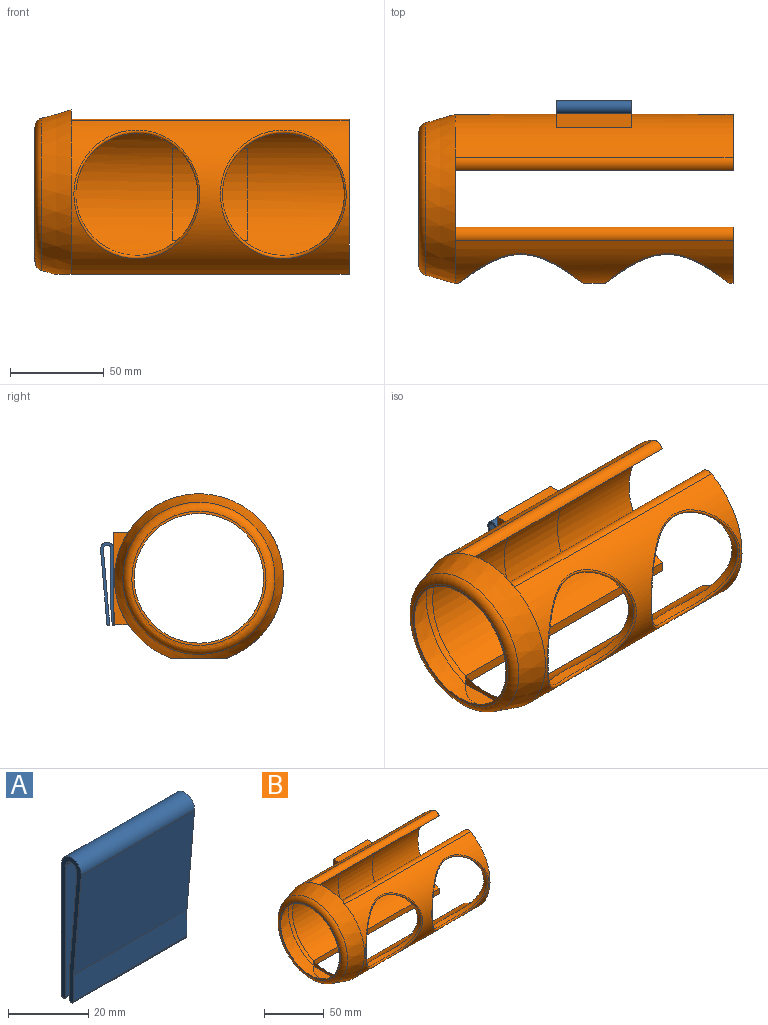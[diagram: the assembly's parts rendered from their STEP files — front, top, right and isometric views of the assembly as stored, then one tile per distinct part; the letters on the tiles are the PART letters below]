
ASSEMBLY  parts=2 mates=1
PART A: 18 faces, bbox 40x7x44.3 mm
  f0: plane 40x15.94mm, normal (0,-1,0), area 637.5mm2, adj f1,f8,f13,f17
  f1: cylinder r=0.75mm len=15.94mm, axis (-1,0,0), area 37.5mm2, adj f0,f2,f13,f17
  f2: plane 40x15.94mm, normal (0,1,0), area 637.5mm2, adj f1,f12,f13,f17
  f3: plane 40x31.9mm, normal (0,-1,-0.08), area 1280.5mm2, adj f4,f12,f13,f14
  f4: plane 40x8.03mm, normal (0,-1,0), area 321.1mm2, adj f3,f5,f13,f14
  f5: cylinder r=0.75mm len=40mm, axis (-1,0,0), area 94.6mm2, adj f4,f6,f13,f14
  f6: plane 40x8.03mm, normal (0,1,0), area 321.1mm2, adj f5,f7,f13,f14
  f7: plane 40x31.97mm, normal (0,1,0.08), area 1283.4mm2, adj f6,f8,f13,f14
  f8: cylinder r=2mm len=40mm, axis (-1,0,0), area 251.3mm2, adj f0,f7,f9,f13,f14,f15
  f9: plane 40x17.26mm, normal (0,-1,0), area 690.4mm2, adj f8,f10,f14,f16
  f10: cylinder r=0.75mm len=17.26mm, axis (-1,0,0), area 40.7mm2, adj f9,f11,f14,f16
  f11: plane 40x17.26mm, normal (0,1,0), area 690.4mm2, adj f10,f12,f14,f16
  f12: cylinder r=3.5mm len=40mm, axis (-1,0,0), area 442.7mm2, adj f2,f3,f11,f13,f14,f15
  f13: plane 44.25x7mm, normal (1,0,0), area 134.9mm2, adj f0,f1,f2,f3,f4,f5,f6,f7
  f14: plane 44.25x7mm, normal (-1,0,0), area 134.9mm2, adj f3,f4,f5,f6,f7,f8,f9,f10
  f15: plane 6.8x1.5mm, normal (0,0,-1), area 10.2mm2, adj f8,f12,f16,f17
  f16: plane 40.75x1.5mm, normal (1,0,0), area 60.9mm2, adj f9,f10,f11,f15
  f17: plane 40.75x1.5mm, normal (-1,0,0), area 60.9mm2, adj f0,f1,f2,f15
PART B: 27 faces, bbox 167.2x90.4x90 mm
  f0: cylinder r=40mm len=148mm, axis (-1,0,0), area 11937.5mm2, adj f8,f9,f12,f15,f26
  f1: cylinder r=45mm len=148mm, axis (-1,0,0), area 13193.9mm2, adj f4,f9,f12,f15,f22,f23,f24,f25
  f2: cylinder r=40mm len=148mm, axis (-1,0,0), area 6613.2mm2, adj f6,f8,f11,f14,f17,f18
  f3: cylinder r=45mm len=148mm, axis (-1,0,0), area 7367.5mm2, adj f4,f6,f11,f14,f19,f20
  f4: cone r=39.5mm half-angle=16deg, axis (1,0,0), area 4173.1mm2, adj f1,f3,f10,f13,f16
  f5: plane 30x5.35mm, normal (1,0,0), area 101.5mm2, adj f8,f11,f12,f13
  f6: plane 82.36x30.02mm, normal (1,0,0), area 502.8mm2, adj f2,f3,f11,f14
  f7: plane 71.46x71.46mm, normal (-1,0,0), area 271.3mm2, adj f8,f16
  f8: cone r=34.5mm half-angle=16deg, axis (1,0,0), area 4681mm2, adj f0,f2,f5,f7,f10
  f9: plane 82.36x30.02mm, normal (1,0,0), area 502.8mm2, adj f0,f1,f12,f15
  f10: plane 43.9x7.92mm, normal (1,0,0), area 176.2mm2, adj f4,f8,f14,f15
  f11: plane 148x5.35mm, normal (0,1,0), area 791.1mm2, adj f2,f3,f5,f6
  f12: plane 148x5.35mm, normal (0,-1,0), area 791.1mm2, adj f0,f1,f5,f9
  f13: plane 30.02x9.02mm, normal (0,0,-1), area 178.9mm2, adj f4,f5
  f14: cylinder r=5mm len=148mm, axis (-1,0,0), area 1208.7mm2, adj f2,f3,f6,f10
  f15: cylinder r=5mm len=148mm, axis (-1,0,0), area 1208.7mm2, adj f0,f1,f9,f10
  f16: torus R=35.73mm, axis (-1,0,0), area 1564.4mm2, adj f4,f7
  f17: cylinder r=32.5mm len=65mm, axis (0,1,0), area 892mm2, adj f2,f20
  f18: cylinder r=32.5mm len=65mm, axis (0,1,0), area 912.3mm2, adj f2,f19
  f19: bspline ~68.53x67.02mm, area 432.3mm2, adj f3,f18
  f20: bspline ~68.53x67.02mm, area 432.3mm2, adj f3,f17
  f21: plane 49x40mm, normal (0,1,0), area 1960mm2, adj f22,f23,f24,f25
  f22: plane 49x7.73mm, normal (1,0,0), area 134mm2, adj f1,f21,f23,f25
  f23: plane 40x7.73mm, normal (0,0,-1), area 309mm2, adj f1,f21,f22,f24
  f24: plane 49x7.73mm, normal (-1,0,0), area 134mm2, adj f1,f21,f23,f25
  f25: plane 40x7.58mm, normal (0,0,1), area 303.3mm2, adj f1,f21,f22,f24
  f26: cylinder r=40mm len=49mm, axis (-1,0,0), area 2109.5mm2, adj f0
PLACE A rot(axis=(-1,0,0),4.8deg) t=(21.76,83.31,-14.32)mm
PLACE B t=(1.01,-4.12,-12.16)mm
MATE fastened A.f3 <-> B.f21  axis (0,-1,0) through (41.76,41.28,-4.78)mm
